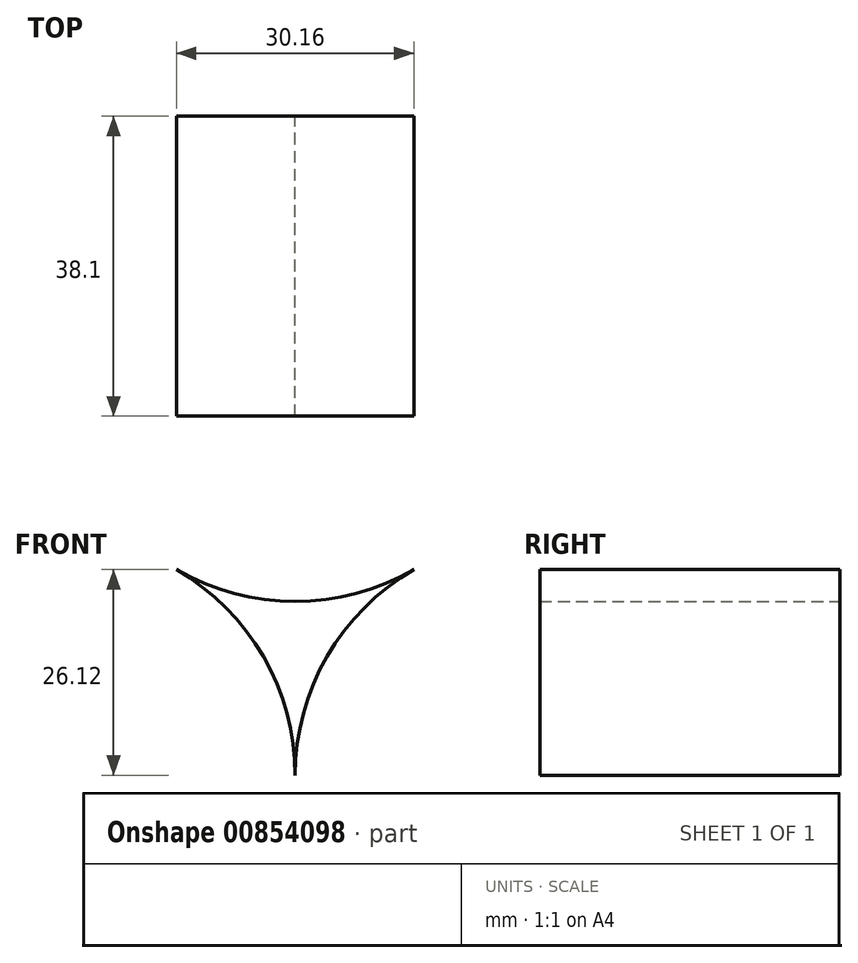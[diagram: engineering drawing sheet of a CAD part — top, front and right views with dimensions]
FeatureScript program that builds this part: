
annotation { "Feature Type Name" : "Feature", "Feature Type Description" : "" }
export const myFeature = defineFeature(function(context is Context, id is Id, definition is map)
    precondition{}
    {
        {
            var Q0;
            Q0=qCreatedBy(makeId("Front.planeOp"),FACE);
            var sketch = newSketch(context, id + "F0", { "sketchPlane" : qUnion([Q0])});
            skCircle(sketch, "E0", {"center": v(0, 0) * mm, "radius": 34.83 * mm});
            skLineSegment(sketch, "E1", {"start": v(0, 0) * mm, "end": v(0, 34.83) * mm});
            skLineSegment(sketch, "E2", {"start": v(0, 0) * mm, "end": v(-30.16, -17.41) * mm});
            skLineSegment(sketch, "E3", {"start": v(0, 0) * mm, "end": v(30.16, -17.41) * mm});
            skCircle(sketch, "E4", {"center": v(-30.16, -17.41) * mm, "radius": 30.16 * mm});
            skCircle(sketch, "E5", {"center": v(0, 34.83) * mm, "radius": 30.16 * mm});
            skCircle(sketch, "E6", {"center": v(30.16, -17.41) * mm, "radius": 30.16 * mm});
            skSolve(sketch);
        }
        {
            var Q0;
            {var subQ0=sQuery(id+"F0.wireOp",EDGE,"E2");var subQ5=sQuery(id+"F0.wireOp",EDGE,"E4");var subQ6=makeQuery(id+"F0.imprint","INTERSECT",VERTEX,{"derivedFrom":[subQ0,subQ5]});Q0=makeQuery(id+"F0.imprint","IMPRINT",FACE,{"disambiguationData":[TD([[makeQuery(id+"F0.imprint","IMPRINT",EDGE,{"disambiguationData":[TD([[subQ6,-1.0]])],"derivedFrom":subQ5}),-1.0]])]});}
            var Q1;
            {var subQ1=sQuery(id+"F0.wireOp",EDGE,"E1");var subQ3=sQuery(id+"F0.wireOp",EDGE,"E5");var subQ4=makeQuery(id+"F0.imprint","INTERSECT",VERTEX,{"derivedFrom":[subQ1,subQ3]});Q1=makeQuery(id+"F0.imprint","IMPRINT",FACE,{"disambiguationData":[TD([[makeQuery(id+"F0.imprint","IMPRINT",EDGE,{"disambiguationData":[TD([[subQ4,-1.0]])],"derivedFrom":subQ3}),-1.0]])]});}
            var Q2;
            {var subQ1=sQuery(id+"F0.wireOp",EDGE,"E2");var subQ3=sQuery(id+"F0.wireOp",EDGE,"E4");var subQ4=makeQuery(id+"F0.imprint","INTERSECT",VERTEX,{"derivedFrom":[subQ1,subQ3]});Q2=makeQuery(id+"F0.imprint","IMPRINT",FACE,{"disambiguationData":[TD([[makeQuery(id+"F0.imprint","IMPRINT",EDGE,{"disambiguationData":[TD([[subQ4,1.0]])],"derivedFrom":subQ3}),-1.0]])]});}
            extrude(context, id + "F1", {"entities" : qUnion([Q0, Q1, Q2]), "depth" : 38.1 * mm, "offsetDistance" : 25.4 * mm});
        }
    });
